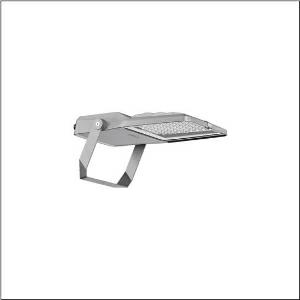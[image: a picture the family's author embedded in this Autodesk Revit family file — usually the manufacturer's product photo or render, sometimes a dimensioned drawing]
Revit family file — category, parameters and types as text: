
# Revit family: floodlight_fl_21_iq_mini___pl61_5xa7772c2c1a_b30e
name_source: partatom
category: Lighting Fixtures
units: mm (PartAtom-declared; Revit-internal decimal feet)

## family parameters
Cut with Voids When Loaded = No
Host = Face
Light Source = No
Part Type = Normal
Room Calculation Point = No
Round Connector Dimension = Use Diameter
Shared = No

## types (1)
- --- (1 x LED, 11980 lm, 87.2 W, 3000K)
    Apparent Load = 87 VA
    CIE Flux Codes = 33 65 98 100 100
    Color Rendering = 70
    Color Temperature = 3000K
    Default Elevation = 1800 mm
    Description = Floodlight FL 21 iQ mini, floodlight, primary light control with lens, of PMMA, primary optical cover: protective disc, of toughened safety glass, transparent, light distribution: PL61, light emission: direct distribution, installation type: surface-mounted, lamps: LED, High Power LED, rated values: 11.980lm | 87,2W | 137,4lm/W (begin service life); end service life: 11.980lm | 92,1W; at 50% lumin. flux: 5.990lm | 40,1W | 149,4lm/W, colour temperature: 3000K, colour rendering: CRI > 70, light colour: 730, light setting 1 begin service life: 100% | 11.980lm | 87,2W | 137,4lm/W | 3.000K, light setting 1 end service life: 92,1W, further light settings possible, control: Street-Remote, Auto-Match, Temp-Guard, Night-Set, Smart-Wire, Desk-Remote (wireless, voltage-free reading and setting of iQ features in the workshop via application-optimized NFC function/RFID function), optimised constant luminous flux control (CLO 2.0), pre-setting: linear dimming characteristic, with terminal, 6-pole, mains connection: 220..240V, AC, 50/60Hz, luminaire housing, of diecast aluminium, powder-coated, SITECO metallic grey (DB 702S), corrosivity category C5 mid according to DIN EN ISO 12944suitable for swimming poolschlorine-resistant, sealing non-destructively replaceable, mounting bracket, of steel, galvanised, powder-coated, SITECO metallic grey (DB 702S), protection rating (complete): IP66, insulation class (complete): insulation class II (safety insulation), certification: CE, ENEC, VDE, protection symbol: D, impact resistance: IK08, permissible operating ambient temperature: -40..+40°C, permissible operating ambient temperature for outdoor applications: -40..+50°C, standard: DIN EN 12944, LABS conformity tested according to VDMA 24364:2018-05, packaging unit: 1 piece

Light Distribution: PL61
    Height = 70 mm
    Lamp = 1 x LED
    Lamp Light Flux = 11980 lm
    Lamp Power = 87.2 W
    Lamp count = 1
    Length = 485 mm
    Luminous efficacy = 137 lm/W
    Manufacturer = Siteco
    ModVariant = No
    Model = 5XA7772C2C1A
    Number of Poles = 1
    OnlyDefault = Yes
    Power Factor = 1
    Product Name = Floodlight FL 21 iQ mini | PL61
    Product group = floodlight | pylon annexe
    ProductGroupID = 6201
    Protection Class = Protection class II
    Protection Degree = IP 66
    RLX_Detail_Level = 1
    RLX_Emergency_Light_Flux = 0 lm
    RLX_Emergency_Type = 0
    RLX_Emergency_Type_DB = No
    RlxData = <blob elided: 96721 chars, md5=1d91c144>
    Socket = socket
    Standby Power = 0 W
    System Light Flux = 11980 lm
    System Power = 87 W
    Type Comments = factory setting: luminous flux: 100 % | dim-lin: 254 | 456 mA
    Type Image = l_1006845.jpg
    URL = http://relux.com
    VarID = @adj_172601
    Voltage = 0 V
    Weight = 0.00 kg
    Width = 337 mm

## geometry (parser evidence)
native form markers: Blend x4, Sweep x15
no freeform markers — native parametric forms only
